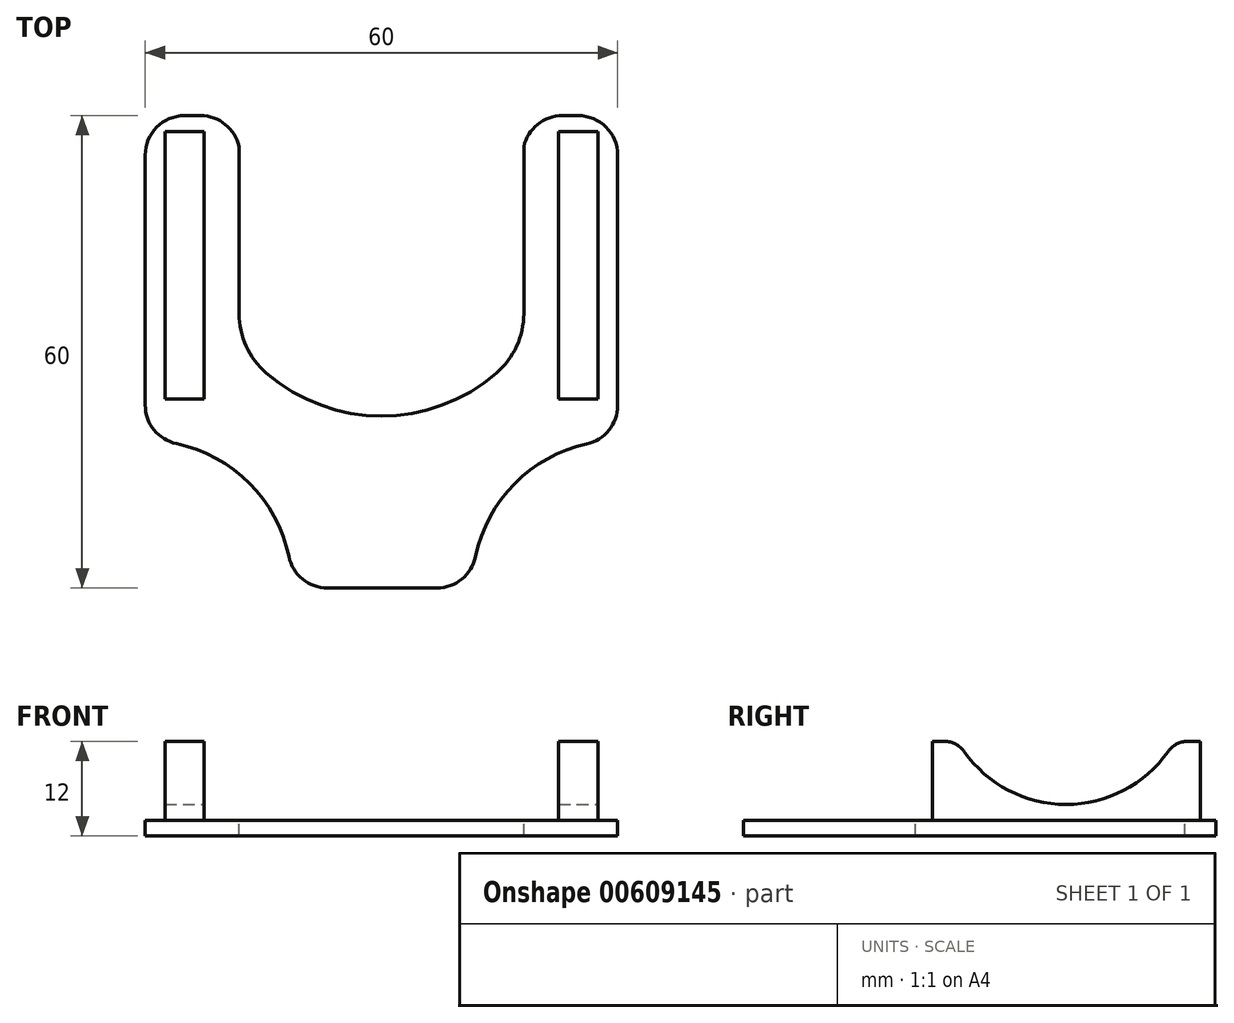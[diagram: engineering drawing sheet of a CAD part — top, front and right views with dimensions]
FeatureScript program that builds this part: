
annotation { "Feature Type Name" : "Feature", "Feature Type Description" : "" }
export const myFeature = defineFeature(function(context is Context, id is Id, definition is map)
    precondition{}
    {
        {
            var Q0;
            Q0=qCreatedBy(makeId("Top.planeOp"),FACE);
            var sketch = newSketch(context, id + "F0", { "sketchPlane" : qUnion([Q0])});
            skLineSegment(sketch, "E0.bottom", {"start": v(-30, 30) * mm, "end": v(30, 30) * mm});
            skLineSegment(sketch, "E0.top", {"start": v(-30, -30) * mm, "end": v(30, -30) * mm});
            skLineSegment(sketch, "E0.left", {"start": v(-30, 30) * mm, "end": v(-30, -30) * mm});
            skLineSegment(sketch, "E0.right", {"start": v(30, 30) * mm, "end": v(30, -30) * mm});
            skSolve(sketch);
        }
        {
            var Q0;
            Q0=makeQuery(id+"F0.imprint","IMPRINT",FACE,{"disambiguationData":[TD([[makeQuery(id+"F0.imprint","IMPRINT",EDGE,{"derivedFrom":sQuery(id+"F0.wireOp",EDGE,"E0.bottom")}),-1.0]])]});
            extrude(context, id + "F1", {"entities" : qUnion([Q0]), "oppositeDirection" : true, "depth" : 2 * mm, "offsetDistance" : 25 * mm});
        }
        {
            var Q0;
            Q0=makeQuery(id+"F1.opExtrude","CAP_FACE",FACE,{"disambiguationData":[OSD([sQuery(id+"F0.wireOp",EDGE,"E0.bottom"),sQuery(id+"F0.wireOp",EDGE,"E0.top"),sQuery(id+"F0.wireOp",EDGE,"E0.left"),sQuery(id+"F0.wireOp",EDGE,"E0.right")])],"isStart":true});
            var sketch = newSketch(context, id + "F2", { "sketchPlane" : qUnion([Q0])});
            skLineSegment(sketch, "E1.bottom", {"start": v(-27.5, 28) * mm, "end": v(-22.5, 28) * mm});
            skLineSegment(sketch, "E1.top", {"start": v(-27.5, -6) * mm, "end": v(-22.5, -6) * mm});
            skLineSegment(sketch, "E1.left", {"start": v(-27.5, 28) * mm, "end": v(-27.5, -6) * mm});
            skLineSegment(sketch, "E1.right", {"start": v(-22.5, 28) * mm, "end": v(-22.5, -6) * mm});
            skLineSegment(sketch, "E2.bottom", {"start": v(22.5, 28) * mm, "end": v(27.5, 28) * mm});
            skLineSegment(sketch, "E2.top", {"start": v(22.5, -6) * mm, "end": v(27.5, -6) * mm});
            skLineSegment(sketch, "E2.left", {"start": v(22.5, 28) * mm, "end": v(22.5, -6) * mm});
            skLineSegment(sketch, "E2.right", {"start": v(27.5, 28) * mm, "end": v(27.5, -6) * mm});
            skSolve(sketch);
        }
        {
            var Q0;
            Q0=makeQuery(id+"F2.imprint","IMPRINT",FACE,{"disambiguationData":[TD([[makeQuery(id+"F2.imprint","IMPRINT",EDGE,{"derivedFrom":sQuery(id+"F2.wireOp",EDGE,"E1.bottom")}),-1.0]])]});
            var Q1;
            Q1=makeQuery(id+"F2.imprint","IMPRINT",FACE,{"disambiguationData":[TD([[makeQuery(id+"F2.imprint","IMPRINT",EDGE,{"derivedFrom":sQuery(id+"F2.wireOp",EDGE,"E2.bottom")}),-1.0]])]});
            extrude(context, id + "F3", {"entities" : qUnion([Q0, Q1]), "operationType" : NewBodyOperationType.ADD, "depth" : 10 * mm, "offsetDistance" : 25 * mm});
        }
        {
            var Q0;
            Q0=qCreatedBy(makeId("Right.planeOp"),FACE);
            var sketch = newSketch(context, id + "F4", { "sketchPlane" : qUnion([Q0])});
            skCircle(sketch, "E3", {"center": v(10.97, 17.85) * mm, "radius": 15.85 * mm});
            skSolve(sketch);
        }
        {
            var Q0;
            Q0=makeQuery(id+"F4.imprint","IMPRINT",FACE,{"disambiguationData":[TD([[makeQuery(id+"F4.imprint","IMPRINT",EDGE,{"derivedFrom":sQuery(id+"F4.wireOp",EDGE,"E3")}),1.0]])]});
            extrude(context, id + "F5", {"entities" : qUnion([Q0]), "operationType" : NewBodyOperationType.REMOVE, "endBound" : BoundingType.SYMMETRIC, "oppositeDirection" : true, "depth" : 60 * mm, "offsetDistance" : 25 * mm});
        }
        {
            var Q0;
            Q0=qCreatedBy(makeId("Top.planeOp"),FACE);
            var sketch = newSketch(context, id + "F6", { "sketchPlane" : qUnion([Q0])});
            skCircle(sketch, "E4", {"center": v(-29.87, -29.77) * mm, "radius": 18.5 * mm});
            skCircle(sketch, "E5", {"center": v(30.07, -29.77) * mm, "radius": 18.5 * mm});
            skCircle(sketch, "E6", {"center": v(0, 29.97) * mm, "radius": 18.5 * mm});
            skSolve(sketch);
        }
        {
            var Q0;
            Q0=makeQuery(id+"F6.imprint","IMPRINT",FACE,{"disambiguationData":[TD([[makeQuery(id+"F6.imprint","IMPRINT",EDGE,{"derivedFrom":sQuery(id+"F6.wireOp",EDGE,"E4")}),1.0]])]});
            var Q1;
            Q1=makeQuery(id+"F6.imprint","IMPRINT",FACE,{"disambiguationData":[TD([[makeQuery(id+"F6.imprint","IMPRINT",EDGE,{"derivedFrom":sQuery(id+"F6.wireOp",EDGE,"E6")}),1.0]])]});
            var Q2;
            Q2=makeQuery(id+"F6.imprint","IMPRINT",FACE,{"disambiguationData":[TD([[makeQuery(id+"F6.imprint","IMPRINT",EDGE,{"derivedFrom":sQuery(id+"F6.wireOp",EDGE,"E5")}),1.0]])]});
            extrude(context, id + "F7", {"entities" : qUnion([Q0, Q1, Q2]), "operationType" : NewBodyOperationType.REMOVE, "oppositeDirection" : true, "depth" : 3.5 * mm, "offsetDistance" : 25 * mm});
        }
        {
            var Q0;
            Q0=makeQuery(id+"F7.boolean.opBoolean","INTERSECT",EDGE,{"derivedFrom":[makeQuery(id+"F1.opExtrude","SWEPT_FACE",FACE,{"disambiguationData":[OSD([sQuery(id+"F0.wireOp",EDGE,"E0.left")])]}),makeQuery(id+"F7.opExtrude","SWEPT_FACE",FACE,{"disambiguationData":[OSD([sQuery(id+"F6.wireOp",EDGE,"E4")])]})]});
            var Q1;
            Q1=makeQuery(id+"F7.boolean.opBoolean","INTERSECT",EDGE,{"derivedFrom":[makeQuery(id+"F1.opExtrude","SWEPT_FACE",FACE,{"disambiguationData":[OSD([sQuery(id+"F0.wireOp",EDGE,"E0.top")])]}),makeQuery(id+"F7.opExtrude","SWEPT_FACE",FACE,{"disambiguationData":[OSD([sQuery(id+"F6.wireOp",EDGE,"E4")])]})]});
            var Q2;
            Q2=makeQuery(id+"F7.boolean.opBoolean","INTERSECT",EDGE,{"derivedFrom":[makeQuery(id+"F1.opExtrude","SWEPT_FACE",FACE,{"disambiguationData":[OSD([sQuery(id+"F0.wireOp",EDGE,"E0.top")])]}),makeQuery(id+"F7.opExtrude","SWEPT_FACE",FACE,{"disambiguationData":[OSD([sQuery(id+"F6.wireOp",EDGE,"E5")])]})]});
            var Q3;
            Q3=makeQuery(id+"F7.boolean.opBoolean","INTERSECT",EDGE,{"derivedFrom":[makeQuery(id+"F1.opExtrude","SWEPT_FACE",FACE,{"disambiguationData":[OSD([sQuery(id+"F0.wireOp",EDGE,"E0.right")])]}),makeQuery(id+"F7.opExtrude","SWEPT_FACE",FACE,{"disambiguationData":[OSD([sQuery(id+"F6.wireOp",EDGE,"E5")])]})]});
            var Q4;
            Q4=makeQuery(id+"F1.opExtrude","SWEPT_EDGE",EDGE,{"disambiguationData":[OSD([sQuery(id+"F0.wireOp",EDGE,"E0.bottom"),sQuery(id+"F0.wireOp",EDGE,"E0.right")])]});
            var Q5;
            Q5=makeQuery(id+"F7.boolean.opBoolean","INTERSECT",EDGE,{"disambiguationData":[OD(0.0)],"derivedFrom":[makeQuery(id+"F1.opExtrude","SWEPT_FACE",FACE,{"disambiguationData":[OSD([sQuery(id+"F0.wireOp",EDGE,"E0.bottom")])]}),makeQuery(id+"F7.opExtrude","SWEPT_FACE",FACE,{"disambiguationData":[OSD([sQuery(id+"F6.wireOp",EDGE,"E6")])]})]});
            var Q6;
            Q6=makeQuery(id+"F7.boolean.opBoolean","INTERSECT",EDGE,{"disambiguationData":[OD(1.0)],"derivedFrom":[makeQuery(id+"F1.opExtrude","SWEPT_FACE",FACE,{"disambiguationData":[OSD([sQuery(id+"F0.wireOp",EDGE,"E0.bottom")])]}),makeQuery(id+"F7.opExtrude","SWEPT_FACE",FACE,{"disambiguationData":[OSD([sQuery(id+"F6.wireOp",EDGE,"E6")])]})]});
            var Q7;
            Q7=makeQuery(id+"F1.opExtrude","SWEPT_EDGE",EDGE,{"disambiguationData":[OSD([sQuery(id+"F0.wireOp",EDGE,"E0.bottom"),sQuery(id+"F0.wireOp",EDGE,"E0.left")])]});
            fillet(context, id + "F8", {"entities" : qUnion([Q0, Q1, Q2, Q3, Q4, Q5, Q6, Q7]), "radius" : 5 * mm, "tangentPropagation" : true, "allowEdgeOverflow" : false});
        }
        {
            var Q0;
            Q0=makeQuery(id+"F1.opExtrude","CAP_FACE",FACE,{"disambiguationData":[OSD([sQuery(id+"F0.wireOp",EDGE,"E0.bottom"),sQuery(id+"F0.wireOp",EDGE,"E0.top"),sQuery(id+"F0.wireOp",EDGE,"E0.left"),sQuery(id+"F0.wireOp",EDGE,"E0.right")])],"isStart":true});
            var sketch = newSketch(context, id + "F9", { "sketchPlane" : qUnion([Q0])});
            skLineSegment(sketch, "E7.bottom", {"start": v(18.08, 26.06) * mm, "end": v(-18.08, 26.06) * mm});
            skLineSegment(sketch, "E7.left", {"start": v(18.08, 26.06) * mm, "end": v(18.08, 1.06) * mm});
            skLineSegment(sketch, "E7.right", {"start": v(-18.08, 26.06) * mm, "end": v(-18.08, 1.06) * mm});
            skPoint(sketch, "E7.middle", {"position": v(0, 0) * mm});
            skArc(sketch, "E8", {"start": v(-18.08, 1.06) * mm, "mid": v(0, -8.16) * mm, "end": v(18.08, 1.06) * mm});
            skSolve(sketch);
        }
        {
            var Q0;
            {var subQ0=sQuery(id+"F9.wireOp",EDGE,"9oqrFMwZ-9BlM-4q9X-Yjdf-Vu79R2wabItX.left");Q0=makeQuery(id+"F9.imprint","IMPRINT",FACE,{"disambiguationData":[TD([[makeQuery(id+"F9.imprint","IMPRINT",EDGE,{"derivedFrom":subQ0}),1.0]])]});}
            var Q1;
            Q1=makeQuery(id+"F9.imprint","IMPRINT",FACE,{"disambiguationData":[TD([[makeQuery(id+"F9.imprint","IMPRINT",EDGE,{"derivedFrom":sQuery(id+"F9.wireOp",EDGE,"E7.left")}),-1.0]])]});
            extrude(context, id + "F10", {"entities" : qUnion([Q0, Q1]), "operationType" : NewBodyOperationType.REMOVE, "oppositeDirection" : true, "depth" : 4 * mm, "offsetDistance" : 25 * mm});
        }
        {
            var Q0;
            Q0=makeQuery(id+"F10.boolean.opBoolean","COPY",EDGE,{"derivedFrom":makeQuery(id+"F10.opExtrude","SWEPT_EDGE",EDGE,{"disambiguationData":[OSD([sQuery(id+"F9.wireOp",EDGE,"E7.right"),sQuery(id+"F9.wireOp",EDGE,"E8")])]})});
            var Q1;
            Q1=makeQuery(id+"F10.boolean.opBoolean","COPY",EDGE,{"derivedFrom":makeQuery(id+"F10.opExtrude","SWEPT_EDGE",EDGE,{"disambiguationData":[OSD([sQuery(id+"F9.wireOp",EDGE,"E7.left"),sQuery(id+"F9.wireOp",EDGE,"E8")])]})});
            fillet(context, id + "F11", {"entities" : qUnion([Q0, Q1]), "radius" : 10 * mm, "tangentPropagation" : true, "allowEdgeOverflow" : false});
        }
        {
            var Q0;
            Q0=makeQuery(id+"F5.boolean.opBoolean","INTERSECT",EDGE,{"disambiguationData":[OD(0.0)],"derivedFrom":[makeQuery(id+"F3.opExtrude","CAP_FACE",FACE,{"disambiguationData":[OSD([sQuery(id+"F2.wireOp",EDGE,"E1.bottom"),sQuery(id+"F2.wireOp",EDGE,"E1.top"),sQuery(id+"F2.wireOp",EDGE,"E1.left"),sQuery(id+"F2.wireOp",EDGE,"E1.right")])],"isStart":false}),makeQuery(id+"F5.opExtrude","SWEPT_FACE",FACE,{"disambiguationData":[OSD([sQuery(id+"F4.wireOp",EDGE,"E3")])]})]});
            var Q1;
            Q1=makeQuery(id+"F5.boolean.opBoolean","INTERSECT",EDGE,{"disambiguationData":[OD(0.0)],"derivedFrom":[makeQuery(id+"F3.opExtrude","CAP_FACE",FACE,{"disambiguationData":[OSD([sQuery(id+"F2.wireOp",EDGE,"E2.bottom"),sQuery(id+"F2.wireOp",EDGE,"E2.top"),sQuery(id+"F2.wireOp",EDGE,"E2.left"),sQuery(id+"F2.wireOp",EDGE,"E2.right")])],"isStart":false}),makeQuery(id+"F5.opExtrude","SWEPT_FACE",FACE,{"disambiguationData":[OSD([sQuery(id+"F4.wireOp",EDGE,"E3")])]})]});
            var Q2;
            Q2=makeQuery(id+"F5.boolean.opBoolean","INTERSECT",EDGE,{"disambiguationData":[OD(1.0)],"derivedFrom":[makeQuery(id+"F3.opExtrude","CAP_FACE",FACE,{"disambiguationData":[OSD([sQuery(id+"F2.wireOp",EDGE,"E2.bottom"),sQuery(id+"F2.wireOp",EDGE,"E2.top"),sQuery(id+"F2.wireOp",EDGE,"E2.left"),sQuery(id+"F2.wireOp",EDGE,"E2.right")])],"isStart":false}),makeQuery(id+"F5.opExtrude","SWEPT_FACE",FACE,{"disambiguationData":[OSD([sQuery(id+"F4.wireOp",EDGE,"E3")])]})]});
            var Q3;
            Q3=makeQuery(id+"F5.boolean.opBoolean","INTERSECT",EDGE,{"disambiguationData":[OD(1.0)],"derivedFrom":[makeQuery(id+"F3.opExtrude","CAP_FACE",FACE,{"disambiguationData":[OSD([sQuery(id+"F2.wireOp",EDGE,"E1.bottom"),sQuery(id+"F2.wireOp",EDGE,"E1.top"),sQuery(id+"F2.wireOp",EDGE,"E1.left"),sQuery(id+"F2.wireOp",EDGE,"E1.right")])],"isStart":false}),makeQuery(id+"F5.opExtrude","SWEPT_FACE",FACE,{"disambiguationData":[OSD([sQuery(id+"F4.wireOp",EDGE,"E3")])]})]});
            fillet(context, id + "F12", {"entities" : qUnion([Q0, Q1, Q2, Q3]), "radius" : 3 * mm, "tangentPropagation" : true, "allowEdgeOverflow" : false});
        }
    });
